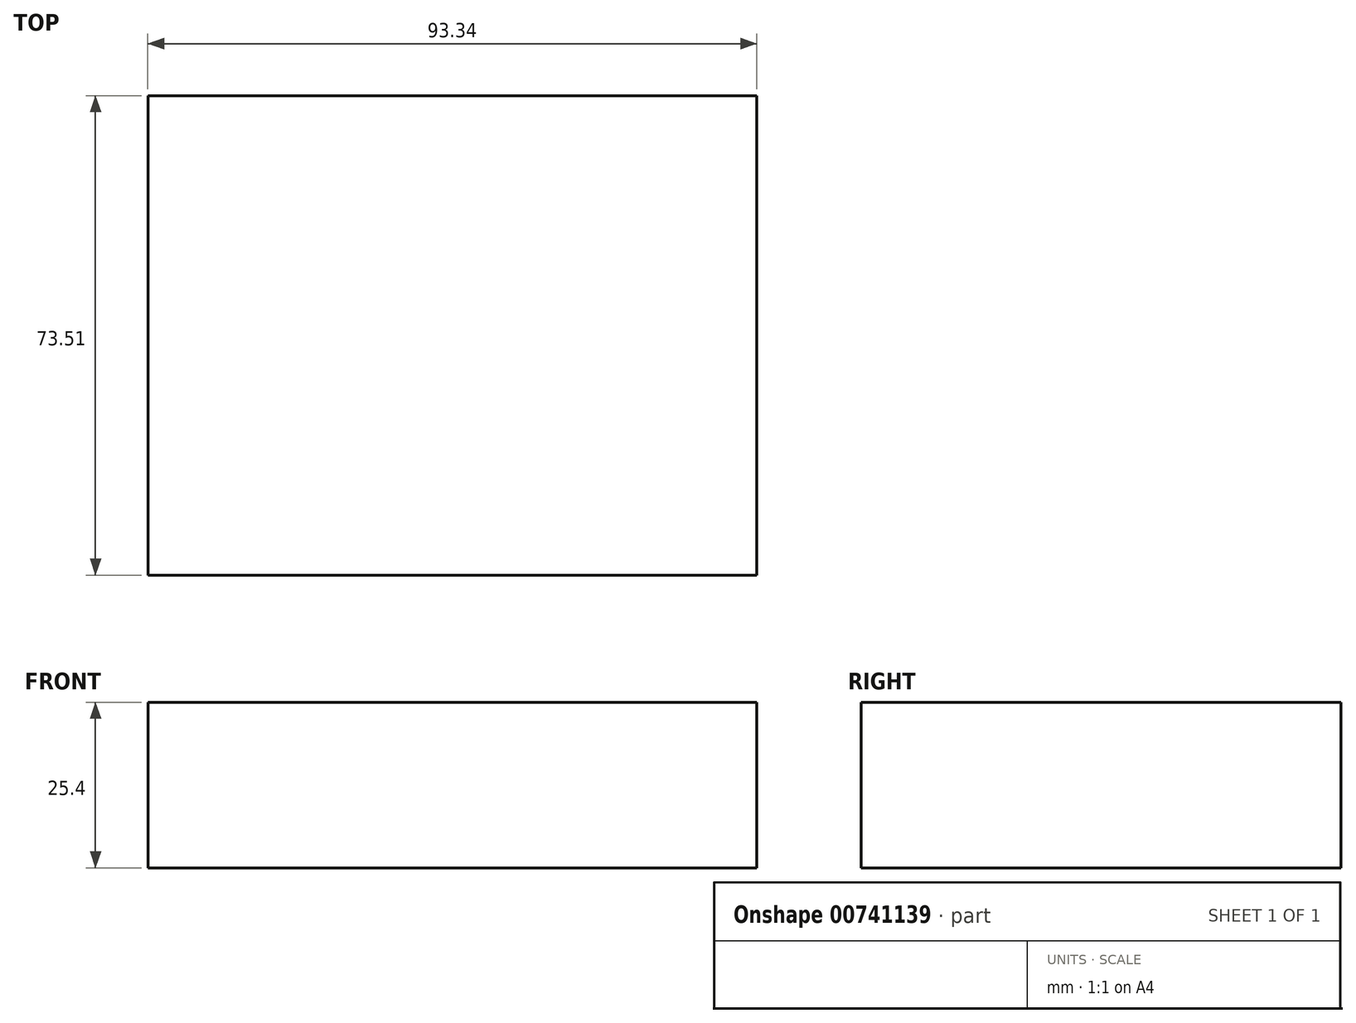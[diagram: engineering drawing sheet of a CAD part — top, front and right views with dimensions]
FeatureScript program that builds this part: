
annotation { "Feature Type Name" : "Feature", "Feature Type Description" : "" }
export const myFeature = defineFeature(function(context is Context, id is Id, definition is map)
    precondition{}
    {
        {
            var Q0;
            Q0=qCreatedBy(makeId("Top.planeOp"),FACE);
            var sketch = newSketch(context, id + "F0", { "sketchPlane" : qUnion([Q0])});
            skLineSegment(sketch, "E0.bottom", {"start": v(-48.28, 46.24) * mm, "end": v(45.06, 46.24) * mm});
            skLineSegment(sketch, "E0.top", {"start": v(-48.28, -27.27) * mm, "end": v(45.06, -27.27) * mm});
            skLineSegment(sketch, "E0.left", {"start": v(-48.28, 46.24) * mm, "end": v(-48.28, -27.27) * mm});
            skLineSegment(sketch, "E0.right", {"start": v(45.06, 46.24) * mm, "end": v(45.06, -27.27) * mm});
            skSolve(sketch);
        }
        {
            var Q0;
            Q0 = qSketchRegion(id + "F0", true);
            extrude(context, id + "F1", {"entities" : qUnion([Q0]), "depth" : 25.4 * mm, "offsetDistance" : 25.4 * mm});
        }
    });
